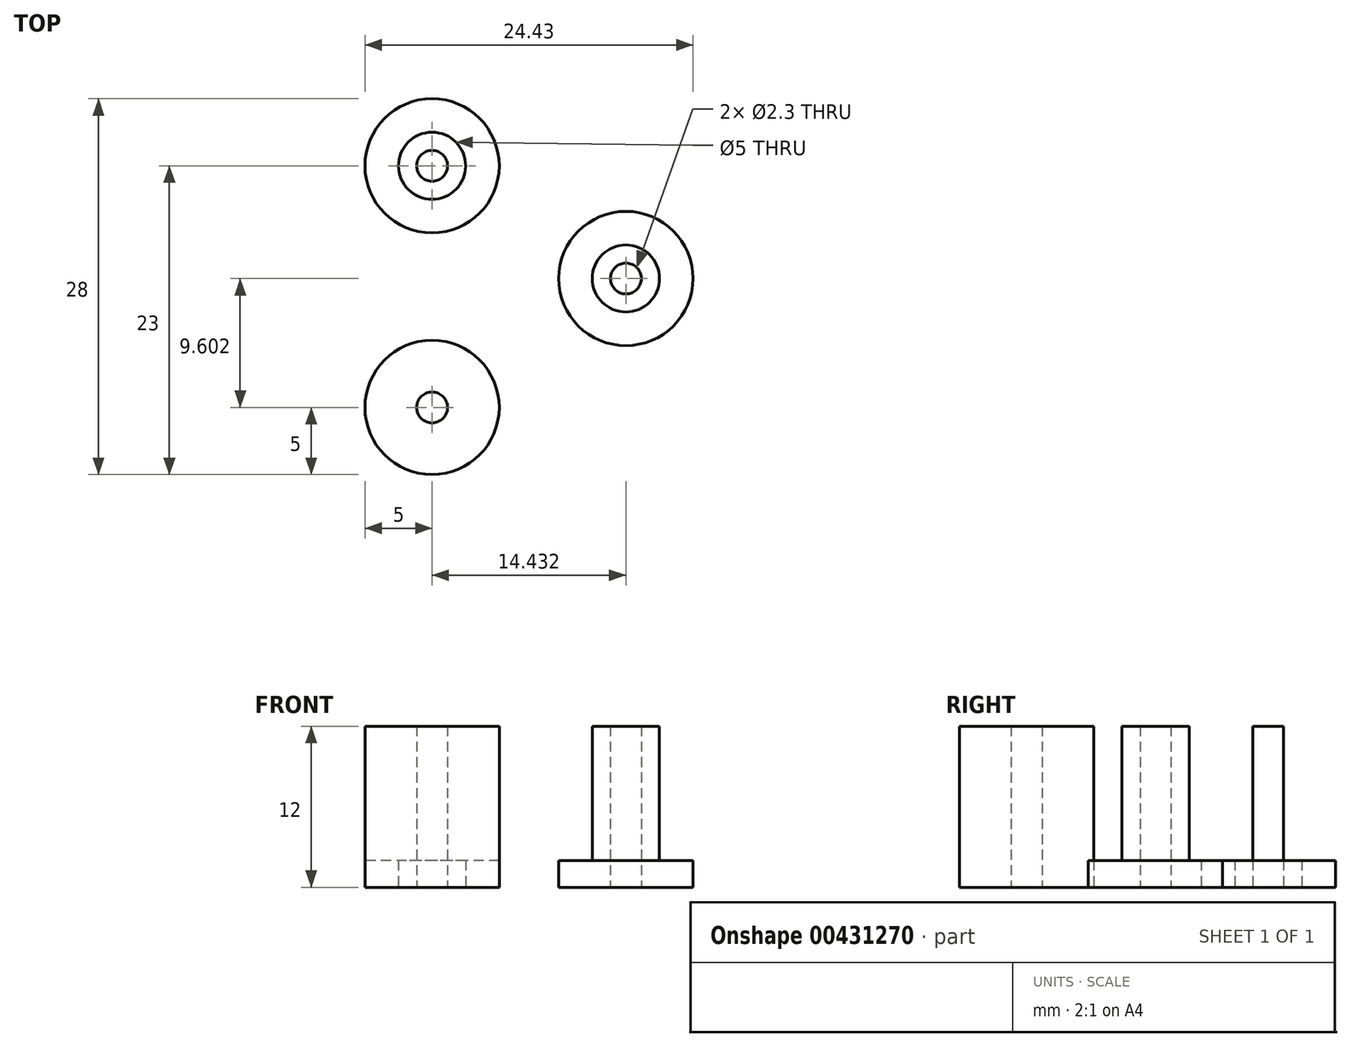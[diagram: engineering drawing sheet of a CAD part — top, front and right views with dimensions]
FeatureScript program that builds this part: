
annotation { "Feature Type Name" : "Feature", "Feature Type Description" : "" }
export const myFeature = defineFeature(function(context is Context, id is Id, definition is map)
    precondition{}
    {
        {
            var Q0;
            Q0=qCreatedBy(makeId("Top.planeOp"),FACE);
            var sketch = newSketch(context, id + "F0", { "sketchPlane" : qUnion([Q0])});
            skLineSegment(sketch, "E0", {"start": v(0, -22.3) * mm, "end": v(0, 22.3) * mm});
            skCircle(sketch, "E1", {"center": v(0, -9) * mm, "radius": 2.5 * mm});
            skCircle(sketch, "E2", {"center": v(0, -9) * mm, "radius": 1.15 * mm});
            skCircle(sketch, "E3", {"center": v(0, 9) * mm, "radius": 2.5 * mm});
            skCircle(sketch, "E4", {"center": v(0, 9) * mm, "radius": 1.15 * mm});
            skLineSegment(sketch, "E5", {"start": v(0, -9) * mm, "end": v(0, 9) * mm});
            skCircle(sketch, "E6", {"center": v(0, -9) * mm, "radius": 5 * mm});
            skCircle(sketch, "E7", {"center": v(0, 9) * mm, "radius": 5 * mm});
            skCircle(sketch, "E8", {"center": v(14.43, 0.6) * mm, "radius": 2.5 * mm});
            skCircle(sketch, "E9", {"center": v(14.43, 0.6) * mm, "radius": 1.15 * mm});
            skCircle(sketch, "E10", {"center": v(14.43, 0.6) * mm, "radius": 5 * mm});
            skSolve(sketch);
        }
        {
            var Q0;
            {var subQ0=sQuery(id+"F0.wireOp",EDGE,"E6");var subQ1=sQuery(id+"F0.wireOp",EDGE,"E0");var subQ2=makeQuery(id+"F0.imprint","INTERSECT",VERTEX,{"derivedFrom":[subQ1,subQ0]});Q0=makeQuery(id+"F0.imprint","IMPRINT",FACE,{"disambiguationData":[TD([[makeQuery(id+"F0.imprint","IMPRINT",EDGE,{"disambiguationData":[TD([[subQ2,-1.0]])],"derivedFrom":subQ1}),-1.0]])]});}
            var Q1;
            {var subQ0=sQuery(id+"F0.wireOp",EDGE,"E6");var subQ1=sQuery(id+"F0.wireOp",EDGE,"E0");var subQ2=makeQuery(id+"F0.imprint","INTERSECT",VERTEX,{"derivedFrom":[subQ1,subQ0]});Q1=makeQuery(id+"F0.imprint","IMPRINT",FACE,{"disambiguationData":[TD([[makeQuery(id+"F0.imprint","IMPRINT",EDGE,{"disambiguationData":[TD([[subQ2,-1.0]])],"derivedFrom":subQ1}),1.0]])]});}
            var Q2;
            {var subQ0=sQuery(id+"F0.wireOp",EDGE,"E1");var subQ1=sQuery(id+"F0.wireOp",EDGE,"E0");var subQ2=makeQuery(id+"F0.imprint","INTERSECT",VERTEX,{"derivedFrom":[subQ1,subQ0]});Q2=makeQuery(id+"F0.imprint","IMPRINT",FACE,{"disambiguationData":[TD([[makeQuery(id+"F0.imprint","IMPRINT",EDGE,{"disambiguationData":[TD([[subQ2,-1.0]])],"derivedFrom":subQ1}),-1.0]])]});}
            var Q3;
            {var subQ0=sQuery(id+"F0.wireOp",EDGE,"E1");var subQ1=sQuery(id+"F0.wireOp",EDGE,"E0");var subQ2=makeQuery(id+"F0.imprint","INTERSECT",VERTEX,{"derivedFrom":[subQ1,subQ0]});Q3=makeQuery(id+"F0.imprint","IMPRINT",FACE,{"disambiguationData":[TD([[makeQuery(id+"F0.imprint","IMPRINT",EDGE,{"disambiguationData":[TD([[subQ2,-1.0]])],"derivedFrom":subQ1}),1.0]])]});}
            var Q4;
            {var subQ0=sQuery(id+"F0.wireOp",EDGE,"E7");var subQ1=sQuery(id+"F0.wireOp",EDGE,"E0");var subQ2=makeQuery(id+"F0.imprint","INTERSECT",VERTEX,{"derivedFrom":[subQ1,subQ0]});Q4=makeQuery(id+"F0.imprint","IMPRINT",FACE,{"disambiguationData":[TD([[makeQuery(id+"F0.imprint","IMPRINT",EDGE,{"disambiguationData":[TD([[subQ2,1.0]])],"derivedFrom":subQ1}),-1.0]])]});}
            var Q5;
            {var subQ0=sQuery(id+"F0.wireOp",EDGE,"E4");var subQ1=sQuery(id+"F0.wireOp",EDGE,"E0");var subQ2=makeQuery(id+"F0.imprint","INTERSECT",VERTEX,{"derivedFrom":[subQ1,subQ0]});Q5=makeQuery(id+"F0.imprint","IMPRINT",FACE,{"disambiguationData":[TD([[makeQuery(id+"F0.imprint","IMPRINT",EDGE,{"disambiguationData":[TD([[subQ2,-1.0]])],"derivedFrom":subQ1}),-1.0]])]});}
            var Q6;
            {var subQ0=sQuery(id+"F0.wireOp",EDGE,"E4");var subQ1=sQuery(id+"F0.wireOp",EDGE,"E0");var subQ2=makeQuery(id+"F0.imprint","INTERSECT",VERTEX,{"derivedFrom":[subQ1,subQ0]});Q6=makeQuery(id+"F0.imprint","IMPRINT",FACE,{"disambiguationData":[TD([[makeQuery(id+"F0.imprint","IMPRINT",EDGE,{"disambiguationData":[TD([[subQ2,-1.0]])],"derivedFrom":subQ1}),1.0]])]});}
            var Q7;
            {var subQ0=sQuery(id+"F0.wireOp",EDGE,"E7");var subQ1=sQuery(id+"F0.wireOp",EDGE,"E0");var subQ2=makeQuery(id+"F0.imprint","INTERSECT",VERTEX,{"derivedFrom":[subQ1,subQ0]});Q7=makeQuery(id+"F0.imprint","IMPRINT",FACE,{"disambiguationData":[TD([[makeQuery(id+"F0.imprint","IMPRINT",EDGE,{"disambiguationData":[TD([[subQ2,1.0]])],"derivedFrom":subQ1}),1.0]])]});}
            var Q8;
            Q8=makeQuery(id+"F0.imprint","IMPRINT",FACE,{"disambiguationData":[TD([[makeQuery(id+"F0.imprint","IMPRINT",EDGE,{"derivedFrom":sQuery(id+"F0.wireOp",EDGE,"E8")}),-1.0]])]});
            var Q9;
            Q9=makeQuery(id+"F0.imprint","IMPRINT",FACE,{"disambiguationData":[TD([[makeQuery(id+"F0.imprint","IMPRINT",EDGE,{"derivedFrom":sQuery(id+"F0.wireOp",EDGE,"E8")}),1.0]])]});
            extrude(context, id + "F1", {"entities" : qUnion([Q0, Q1, Q2, Q3, Q4, Q5, Q6, Q7, Q8, Q9]), "depth" : 2 * mm});
        }
        {
            var Q0;
            {var subQ0=sQuery(id+"F0.wireOp",EDGE,"E1");var subQ1=sQuery(id+"F0.wireOp",EDGE,"E0");var subQ2=makeQuery(id+"F0.imprint","INTERSECT",VERTEX,{"derivedFrom":[subQ1,subQ0]});Q0=makeQuery(id+"F0.imprint","IMPRINT",FACE,{"disambiguationData":[TD([[makeQuery(id+"F0.imprint","IMPRINT",EDGE,{"disambiguationData":[TD([[subQ2,-1.0]])],"derivedFrom":subQ1}),-1.0]])]});}
            var Q1;
            {var subQ0=sQuery(id+"F0.wireOp",EDGE,"E1");var subQ1=sQuery(id+"F0.wireOp",EDGE,"E0");var subQ2=makeQuery(id+"F0.imprint","INTERSECT",VERTEX,{"derivedFrom":[subQ1,subQ0]});Q1=makeQuery(id+"F0.imprint","IMPRINT",FACE,{"disambiguationData":[TD([[makeQuery(id+"F0.imprint","IMPRINT",EDGE,{"disambiguationData":[TD([[subQ2,-1.0]])],"derivedFrom":subQ1}),1.0]])]});}
            var Q2;
            {var subQ0=sQuery(id+"F0.wireOp",EDGE,"E4");var subQ1=sQuery(id+"F0.wireOp",EDGE,"E0");var subQ2=makeQuery(id+"F0.imprint","INTERSECT",VERTEX,{"derivedFrom":[subQ1,subQ0]});Q2=makeQuery(id+"F0.imprint","IMPRINT",FACE,{"disambiguationData":[TD([[makeQuery(id+"F0.imprint","IMPRINT",EDGE,{"disambiguationData":[TD([[subQ2,-1.0]])],"derivedFrom":subQ1}),-1.0]])]});}
            var Q3;
            {var subQ0=sQuery(id+"F0.wireOp",EDGE,"E4");var subQ1=sQuery(id+"F0.wireOp",EDGE,"E0");var subQ2=makeQuery(id+"F0.imprint","INTERSECT",VERTEX,{"derivedFrom":[subQ1,subQ0]});Q3=makeQuery(id+"F0.imprint","IMPRINT",FACE,{"disambiguationData":[TD([[makeQuery(id+"F0.imprint","IMPRINT",EDGE,{"disambiguationData":[TD([[subQ2,-1.0]])],"derivedFrom":subQ1}),1.0]])]});}
            var Q4;
            Q4=makeQuery(id+"F0.imprint","IMPRINT",FACE,{"disambiguationData":[TD([[makeQuery(id+"F0.imprint","IMPRINT",EDGE,{"derivedFrom":sQuery(id+"F0.wireOp",EDGE,"E8")}),1.0]])]});
            extrude(context, id + "F2", {"entities" : qUnion([Q0, Q1, Q2, Q3, Q4]), "operationType" : NewBodyOperationType.ADD, "depth" : 12 * mm});
        }
    });
